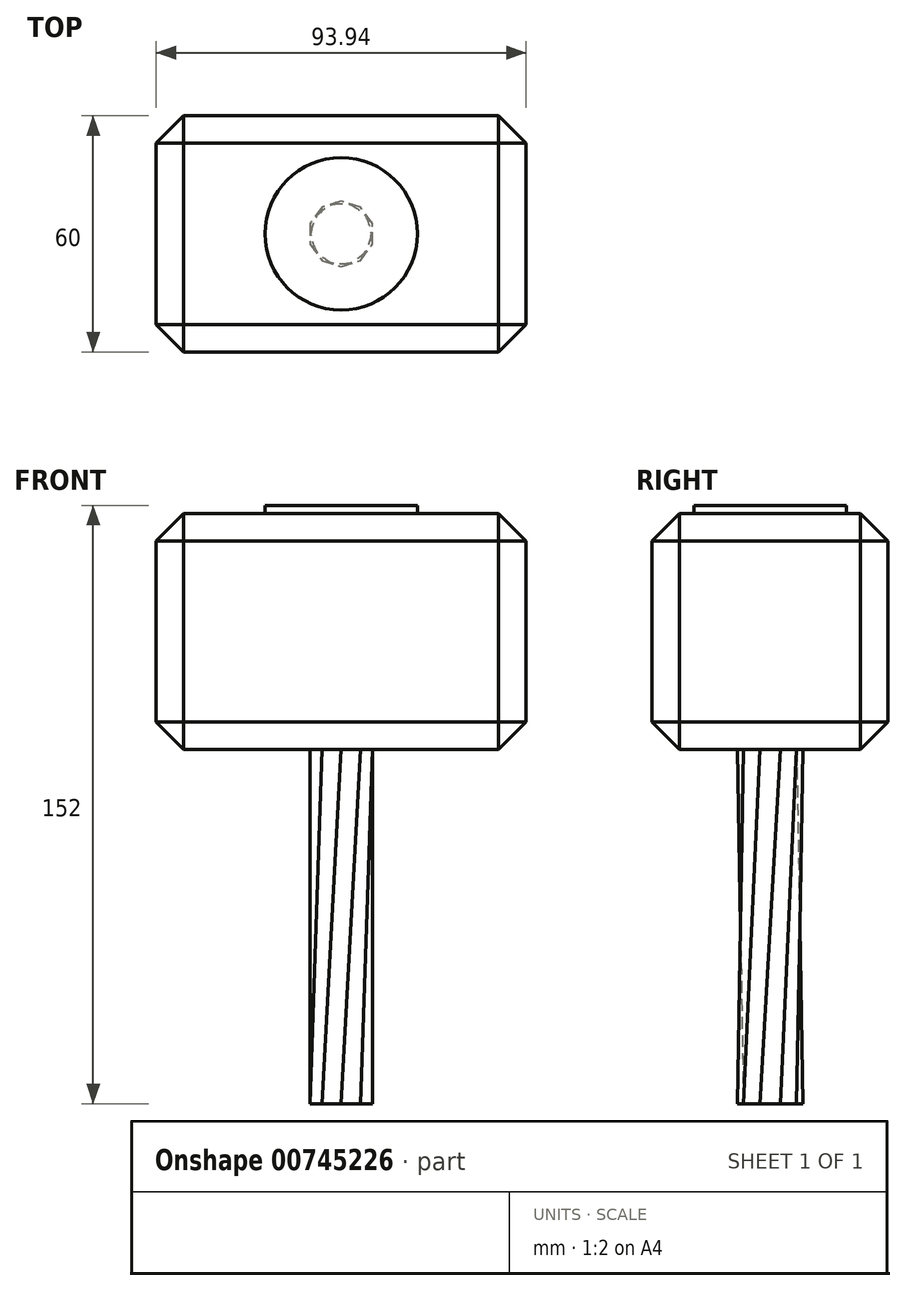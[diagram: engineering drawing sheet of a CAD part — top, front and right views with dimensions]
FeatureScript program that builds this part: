
annotation { "Feature Type Name" : "Feature", "Feature Type Description" : "" }
export const myFeature = defineFeature(function(context is Context, id is Id, definition is map)
    precondition{}
    {
        {
            var Q0;
            Q0=qCreatedBy(makeId("Top.planeOp"),FACE);
            var sketch = newSketch(context, id + "F0", { "sketchPlane" : qUnion([Q0])});
            skLineSegment(sketch, "E0.bottom", {"start": v(46.97, 30) * mm, "end": v(-46.97, 30) * mm});
            skLineSegment(sketch, "E0.top", {"start": v(46.97, -30) * mm, "end": v(-46.97, -30) * mm});
            skLineSegment(sketch, "E0.left", {"start": v(46.97, 30) * mm, "end": v(46.97, -30) * mm});
            skLineSegment(sketch, "E0.right", {"start": v(-46.97, 30) * mm, "end": v(-46.97, -30) * mm});
            skPoint(sketch, "E0.middle", {"position": v(0, 0) * mm});
            skSolve(sketch);
        }
        {
            var Q0;
            Q0=makeQuery(id+"F0.imprint","IMPRINT",FACE,{"disambiguationData":[TD([[makeQuery(id+"F0.imprint","IMPRINT",EDGE,{"derivedFrom":sQuery(id+"F0.wireOp",EDGE,"E0.bottom")}),1.0]])]});
            extrude(context, id + "F1", {"entities" : qUnion([Q0]), "depth" : 30 * mm, "offsetDistance" : 25 * mm});
        }
        {
            var Q0;
            Q0=makeQuery(id+"F1.opExtrude","CAP_EDGE",EDGE,{"disambiguationData":[OSD([sQuery(id+"F0.wireOp",EDGE,"E0.bottom")])],"isStart":false});
            var Q1;
            Q1=makeQuery(id+"F1.opExtrude","CAP_EDGE",EDGE,{"disambiguationData":[OSD([sQuery(id+"F0.wireOp",EDGE,"E0.right")])],"isStart":false});
            var Q2;
            Q2=makeQuery(id+"F1.opExtrude","SWEPT_EDGE",EDGE,{"disambiguationData":[OSD([sQuery(id+"F0.wireOp",EDGE,"E0.bottom"),sQuery(id+"F0.wireOp",EDGE,"E0.right")])]});
            var Q3;
            Q3=makeQuery(id+"F1.opExtrude","CAP_EDGE",EDGE,{"disambiguationData":[OSD([sQuery(id+"F0.wireOp",EDGE,"E0.top")])],"isStart":false});
            var Q4;
            Q4=makeQuery(id+"F1.opExtrude","SWEPT_EDGE",EDGE,{"disambiguationData":[OSD([sQuery(id+"F0.wireOp",EDGE,"E0.top"),sQuery(id+"F0.wireOp",EDGE,"E0.right")])]});
            var Q5;
            Q5=makeQuery(id+"F1.opExtrude","SWEPT_EDGE",EDGE,{"disambiguationData":[OSD([sQuery(id+"F0.wireOp",EDGE,"E0.top"),sQuery(id+"F0.wireOp",EDGE,"E0.left")])]});
            var Q6;
            Q6=makeQuery(id+"F1.opExtrude","SWEPT_EDGE",EDGE,{"disambiguationData":[OSD([sQuery(id+"F0.wireOp",EDGE,"E0.bottom"),sQuery(id+"F0.wireOp",EDGE,"E0.left")])]});
            var Q7;
            Q7=makeQuery(id+"F1.opExtrude","CAP_EDGE",EDGE,{"disambiguationData":[OSD([sQuery(id+"F0.wireOp",EDGE,"E0.left")])],"isStart":false});
            chamfer(context, id + "F2", {"entities" : qUnion([Q0, Q1, Q2, Q3, Q4, Q5, Q6, Q7]), "width" : 7 * mm, "tangentPropagation" : true});
        }
        {
            var Q0;
            Q0=makeQuery(id+"F1.opExtrude","SWEPT_BODY",BODY,{"disambiguationData":[OSD([sQuery(id+"F0.wireOp",EDGE,"E0.bottom"),sQuery(id+"F0.wireOp",EDGE,"E0.top"),sQuery(id+"F0.wireOp",EDGE,"E0.left"),sQuery(id+"F0.wireOp",EDGE,"E0.right")])]});
            var Q1;
            Q1=makeQuery(id+"F1.opExtrude","CAP_FACE",FACE,{"disambiguationData":[OSD([sQuery(id+"F0.wireOp",EDGE,"E0.bottom"),sQuery(id+"F0.wireOp",EDGE,"E0.top"),sQuery(id+"F0.wireOp",EDGE,"E0.left"),sQuery(id+"F0.wireOp",EDGE,"E0.right")])],"isStart":true});
            mirror(context, id + "F3", {"operationType" : NewBodyOperationType.ADD, "entities" : qUnion([Q0]), "mirrorPlane" : qUnion([Q1])});
        }
        {
            var Q0;
            Q0=makeQuery(id+"F1.opExtrude","CAP_FACE",FACE,{"disambiguationData":[OSD([sQuery(id+"F0.wireOp",EDGE,"E0.bottom"),sQuery(id+"F0.wireOp",EDGE,"E0.top"),sQuery(id+"F0.wireOp",EDGE,"E0.left"),sQuery(id+"F0.wireOp",EDGE,"E0.right")])],"isStart":false});
            var sketch = newSketch(context, id + "F4", { "sketchPlane" : qUnion([Q0])});
            skCircle(sketch, "E1", {"center": v(0, 0) * mm, "radius": 19.36 * mm});
            skSolve(sketch);
        }
        {
            var Q0;
            Q0=makeQuery(id+"F4.imprint","IMPRINT",FACE,{"disambiguationData":[TD([[makeQuery(id+"F4.imprint","IMPRINT",EDGE,{"derivedFrom":sQuery(id+"F4.wireOp",EDGE,"E1")}),1.0]])]});
            extrude(context, id + "F5", {"entities" : qUnion([Q0]), "operationType" : NewBodyOperationType.ADD, "depth" : 2 * mm, "offsetDistance" : 25 * mm});
        }
        {
            var Q0;
            Q0=makeQuery(id+"F3.opPattern","COPY",FACE,{"derivedFrom":makeQuery(id+"F1.opExtrude","CAP_FACE",FACE,{"disambiguationData":[OSD([sQuery(id+"F0.wireOp",EDGE,"E0.bottom"),sQuery(id+"F0.wireOp",EDGE,"E0.top"),sQuery(id+"F0.wireOp",EDGE,"E0.left"),sQuery(id+"F0.wireOp",EDGE,"E0.right")])],"isStart":false}),"instanceName":"1"});
            var sketch = newSketch(context, id + "F6", { "sketchPlane" : qUnion([Q0])});
            skCircle(sketch, "E2.cCircle", {"center": v(0, 0) * mm, "radius": 7.93 * mm, "construction": true});
            skLineSegment(sketch, "E2.0", {"start": v(7.93, 2.58) * mm, "end": v(7.93, -2.58) * mm});
            skLineSegment(sketch, "E2.1", {"start": v(7.93, -2.58) * mm, "end": v(4.9, -6.75) * mm});
            skLineSegment(sketch, "E2.2", {"start": v(4.9, -6.75) * mm, "end": v(0, -8.34) * mm});
            skLineSegment(sketch, "E2.3", {"start": v(0, -8.34) * mm, "end": v(-4.9, -6.75) * mm});
            skLineSegment(sketch, "E2.4", {"start": v(-4.9, -6.75) * mm, "end": v(-7.93, -2.58) * mm});
            skLineSegment(sketch, "E2.5", {"start": v(-7.93, -2.58) * mm, "end": v(-7.93, 2.58) * mm});
            skLineSegment(sketch, "E2.6", {"start": v(-7.93, 2.58) * mm, "end": v(-4.9, 6.75) * mm});
            skLineSegment(sketch, "E2.7", {"start": v(-4.9, 6.75) * mm, "end": v(0, 8.34) * mm});
            skLineSegment(sketch, "E2.8", {"start": v(0, 8.34) * mm, "end": v(4.9, 6.75) * mm});
            skLineSegment(sketch, "E2.9", {"start": v(4.9, 6.75) * mm, "end": v(7.93, 2.58) * mm});
            skPoint(sketch, "E2.0.midPoint", {"position": v(7.93, 0) * mm});
            skSolve(sketch);
        }
        {
            var Q0;
            Q0=makeQuery(id+"F6.imprint","IMPRINT",FACE,{"disambiguationData":[TD([[makeQuery(id+"F6.imprint","IMPRINT",EDGE,{"derivedFrom":sQuery(id+"F6.wireOp",EDGE,"E2.0")}),1.0]])]});
            cPlane(context, id + "F7", {"entities" : qUnion([Q0]), "cplaneType" : CPlaneType.OFFSET, "offset" : 90 * mm, "width" : 150 * mm, "height" : 150 * mm});
        }
        {
            var Q0;
            Q0=qCreatedBy(id+"F7.planeOp",FACE);
            var sketch = newSketch(context, id + "F8", { "sketchPlane" : qUnion([Q0])});
            skLineSegment(sketch, "E3.0.0", {"start": v(7.93, 2.58) * mm, "end": v(4.9, 6.75) * mm});
            skLineSegment(sketch, "E3.0.1", {"start": v(4.9, 6.75) * mm, "end": v(0, 8.34) * mm});
            skLineSegment(sketch, "E3.0.2", {"start": v(0, 8.34) * mm, "end": v(-4.9, 6.75) * mm});
            skLineSegment(sketch, "E3.0.3", {"start": v(-4.9, 6.75) * mm, "end": v(-7.93, 2.58) * mm});
            skLineSegment(sketch, "E3.0.4", {"start": v(-7.93, 2.58) * mm, "end": v(-7.93, -2.58) * mm});
            skLineSegment(sketch, "E3.0.5", {"start": v(-7.93, -2.58) * mm, "end": v(-4.9, -6.75) * mm});
            skLineSegment(sketch, "E3.0.6", {"start": v(-4.9, -6.75) * mm, "end": v(0, -8.34) * mm});
            skLineSegment(sketch, "E3.0.7", {"start": v(0, -8.34) * mm, "end": v(4.9, -6.75) * mm});
            skLineSegment(sketch, "E3.0.8", {"start": v(4.9, -6.75) * mm, "end": v(7.93, -2.58) * mm});
            skLineSegment(sketch, "E3.0.9", {"start": v(7.93, -2.58) * mm, "end": v(7.93, 2.58) * mm});
            skSolve(sketch);
        }
        {
            var Q1;
            Q1=makeQuery(id+"F6.imprint","IMPRINT",FACE,{"disambiguationData":[TD([[makeQuery(id+"F6.imprint","IMPRINT",EDGE,{"derivedFrom":sQuery(id+"F6.wireOp",EDGE,"E2.0")}),-1.0]])]});
            var Q2;
            Q2=makeQuery(id+"F8.imprint","IMPRINT",FACE,{"disambiguationData":[TD([[makeQuery(id+"F8.imprint","IMPRINT",EDGE,{"derivedFrom":sQuery(id+"F8.wireOp",EDGE,"E3.0.0")}),1.0]])]});
            var Q3;
            Q3=sQuery(id+"F8.wireOp",VERTEX,"E3.0.0.end");
            var Q4;
            Q4=sQuery(id+"F6.wireOp",VERTEX,"E2.0.start");
            loft(context, id + "F9", {"operationType" : NewBodyOperationType.ADD, "sheetProfilesArray" : [{ "sheetProfileEntities" : qUnion([Q1]) }, { "sheetProfileEntities" : qUnion([Q2]) }], "matchConnections" : true, "connections" : [{ "connectionEntities" : qUnion([Q3, Q4]), "connectionEdgeQueries" : qUnion([]), "connectionEdgeParameters" : [] }]});
        }
    });
